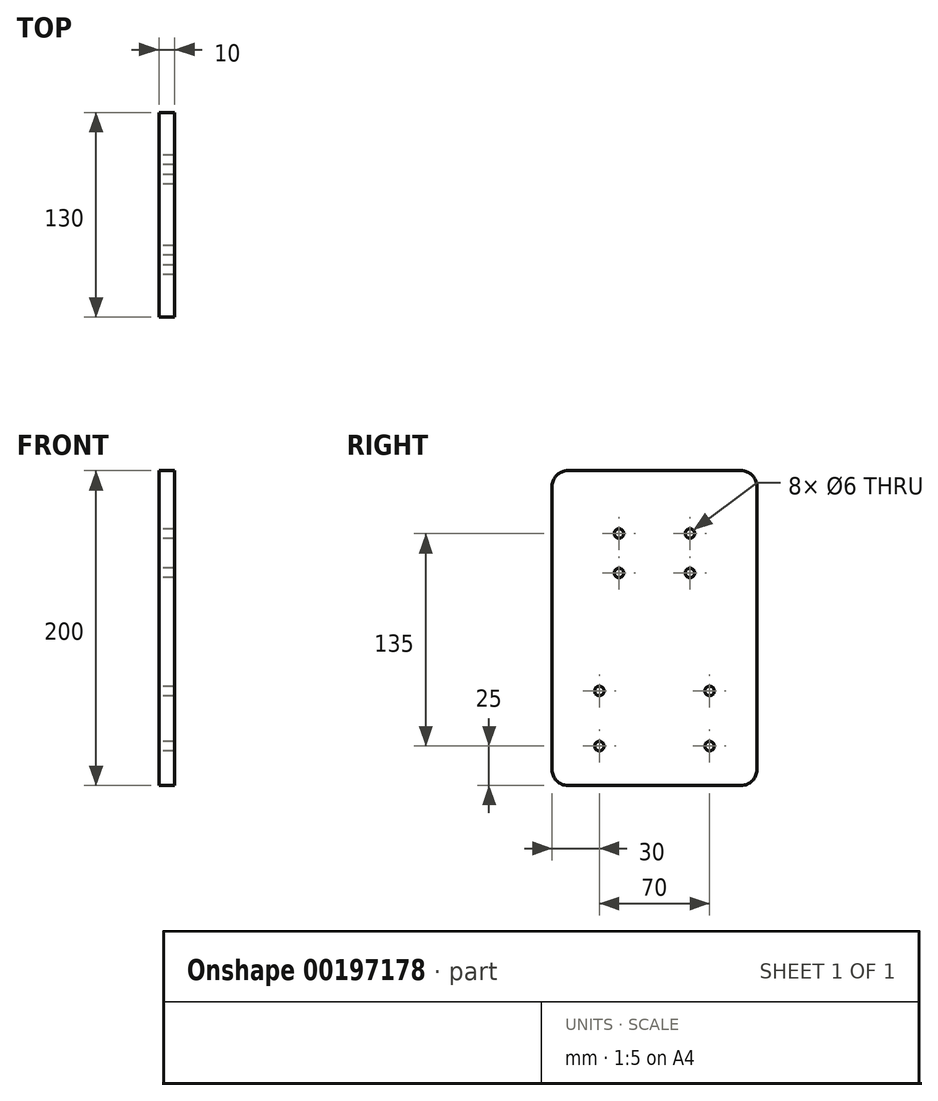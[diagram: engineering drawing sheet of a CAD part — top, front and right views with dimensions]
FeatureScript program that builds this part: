
annotation { "Feature Type Name" : "Feature", "Feature Type Description" : "" }
export const myFeature = defineFeature(function(context is Context, id is Id, definition is map)
    precondition{}
    {
        {
            var Q0;
            Q0=qCreatedBy(makeId("Right.planeOp"),FACE);
            var sketch = newSketch(context, id + "F0", { "sketchPlane" : qUnion([Q0])});
            skLineSegment(sketch, "E0.bottom", {"start": v(-55, 100) * mm, "end": v(55, 100) * mm});
            skLineSegment(sketch, "E0.top", {"start": v(-55, -100) * mm, "end": v(55, -100) * mm});
            skLineSegment(sketch, "E0.left", {"start": v(-65, 90) * mm, "end": v(-65, -90) * mm});
            skLineSegment(sketch, "E0.right", {"start": v(65, 90) * mm, "end": v(65, -90) * mm});
            skPoint(sketch, "E0.middle", {"position": v(0, 0) * mm});
            skPoint(sketch, "E1.visualSharp", {"position": v(-65, 100) * mm});
            skArc(sketch, "E1.filletArc", {"start": v(-55, 100) * mm, "mid": v(-62.07, 97.07) * mm, "end": v(-65, 90) * mm});
            skPoint(sketch, "E2.visualSharp", {"position": v(65, 100) * mm});
            skArc(sketch, "E2.filletArc", {"start": v(65, 90) * mm, "mid": v(62.07, 97.07) * mm, "end": v(55, 100) * mm});
            skPoint(sketch, "E3.visualSharp", {"position": v(65, -100) * mm});
            skArc(sketch, "E3.filletArc", {"start": v(55, -100) * mm, "mid": v(62.07, -97.07) * mm, "end": v(65, -90) * mm});
            skPoint(sketch, "E4.visualSharp", {"position": v(-65, -100) * mm});
            skArc(sketch, "E4.filletArc", {"start": v(-65, -90) * mm, "mid": v(-62.07, -97.07) * mm, "end": v(-55, -100) * mm});
            skLineSegment(sketch, "E5.bottom", {"start": v(-22.5, 60) * mm, "end": v(22.5, 60) * mm, "construction": true});
            skLineSegment(sketch, "E5.top", {"start": v(-22.5, 35) * mm, "end": v(22.5, 35) * mm, "construction": true});
            skLineSegment(sketch, "E5.left", {"start": v(-22.5, 60) * mm, "end": v(-22.5, 35) * mm, "construction": true});
            skLineSegment(sketch, "E5.right", {"start": v(22.5, 60) * mm, "end": v(22.5, 35) * mm, "construction": true});
            skPoint(sketch, "E5.middle", {"position": v(0, 47.5) * mm});
            skLineSegment(sketch, "E6.bottom", {"start": v(-35, -40) * mm, "end": v(35, -40) * mm, "construction": true});
            skLineSegment(sketch, "E6.top", {"start": v(-35, -75) * mm, "end": v(35, -75) * mm, "construction": true});
            skLineSegment(sketch, "E6.left", {"start": v(-35, -40) * mm, "end": v(-35, -75) * mm, "construction": true});
            skLineSegment(sketch, "E6.right", {"start": v(35, -40) * mm, "end": v(35, -75) * mm, "construction": true});
            skPoint(sketch, "E6.middle", {"position": v(0, -57.5) * mm});
            skCircle(sketch, "E7", {"center": v(-35, -40) * mm, "radius": 3 * mm});
            skCircle(sketch, "E8", {"center": v(-35, -75) * mm, "radius": 3 * mm});
            skCircle(sketch, "E9", {"center": v(35, -40) * mm, "radius": 3 * mm});
            skCircle(sketch, "E10", {"center": v(35, -75) * mm, "radius": 3 * mm});
            skCircle(sketch, "E11", {"center": v(-22.5, 60) * mm, "radius": 3 * mm});
            skCircle(sketch, "E12", {"center": v(-22.5, 35) * mm, "radius": 3 * mm});
            skCircle(sketch, "E13", {"center": v(22.5, 35) * mm, "radius": 3 * mm});
            skCircle(sketch, "E14", {"center": v(22.5, 60) * mm, "radius": 3 * mm});
            skSolve(sketch);
        }
        {
            var Q0;
            Q0 = qSketchRegion(id + "F0", true);
            extrude(context, id + "F1", {"entities" : qUnion([Q0]), "depth" : 10 * mm});
        }
    });
